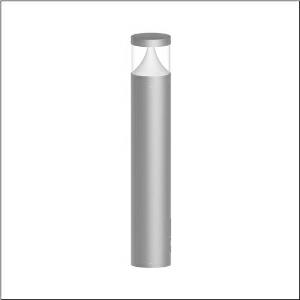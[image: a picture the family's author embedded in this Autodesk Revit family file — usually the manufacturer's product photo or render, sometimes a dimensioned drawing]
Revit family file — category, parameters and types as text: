
# Revit family: cl_31_poller_90_5cl444603
name_source: partatom
category: Lighting Fixtures
units: mm (PartAtom-declared; Revit-internal decimal feet)

## family parameters
Cut with Voids When Loaded = No
Host = Face
Light Source = No
Part Type = Normal
Room Calculation Point = No
Round Connector Dimension = Use Diameter
Shared = No

## types (1)
- --- (1 x LED, 1500 lm, 14 W, 3000K)
    Apparent Load = 14 VA
    CIE Flux Codes = 19 66 88 92 100
    Color Rendering = 80
    Color Temperature = 3000K
    Default Elevation = 1800 mm
    Description = CL 31 Bollard 90, bollard luminaire, primary light control with lens, of PC, primary optical cover: cover panel, of PC, transparent, secondary light control with reflector, of PC, primary light characteristic: asymmetric, LED, rated luminous flux: 1.500lm, luminous efficacy: 107lm/W, light colour: 830, colour temperature: 3000K, control gear: DALI, with terminal, 5-pole, max. 2.5mm², mains connection: 220..240V, AC, 50/60Hz, rated input power: 14W, luminaire housing, of aluminium, powder-coated, Siteco® metallic grey, diameter: 170mm, height: 900mm, protection rating (complete): IP65, insulation class (complete): insulation class I (protective earthing), certification: CE, ENEC, impact resistance: IK10, permissible operating ambient temperature for outdoor applications: -20..+50°C, packaging unit: 1 piece
    Height = 200 mm  [stored 0.656168 ft]
    Lamp = 1 x LED
    Lamp Light Flux = 1500 lm
    Lamp Power = 14 W
    Lamp count = 1
    Length = 170 mm  [stored 0.557743 ft]
    Luminous efficacy = 107 lm/W
    Manufacturer = Siteco
    ModVariant = No
    Model = 5CL444603
    Mounting Place = Floor
    Mounting Type = Freestanding
    Number of Poles = 1
    OnlyDefault = Yes
    Power Factor = 1
    Product Name = CL 31 Poller 90
    Product group = bollard luminaire
    ProductGroupID = 1304
    Protection Class = Protection class I
    Protection Degree = IP 65
    RLX_Detail_Level = 1
    RLX_Emergency_Light_Flux = 0 lm
    RLX_Emergency_Type = 0
    RLX_Emergency_Type_DB = No
    RlxData = <blob elided: 64649 chars, md5=45c48f38>
    Socket = socket
    Standby Power = 0 W
    System Light Flux = 1500 lm
    System Power = 14 W
    Type Comments = factory setting: luminous flux: 100 % | dim-lin: 254 | 350 mA
    Type Image = l_1006899.jpg
    URL = http://relux.com
    VarID = @adj_216535
    Voltage = 0 V
    Weight = 0.00 kg
    Width = 0 mm  [stored 0 ft]

note: [stored X ft] marks values corroborated as IEEE doubles in the binary element streams (Revit-internal decimal feet)

## geometry (parser evidence)
native form markers: Blend x4, Sweep x9
no freeform markers — native parametric forms only
